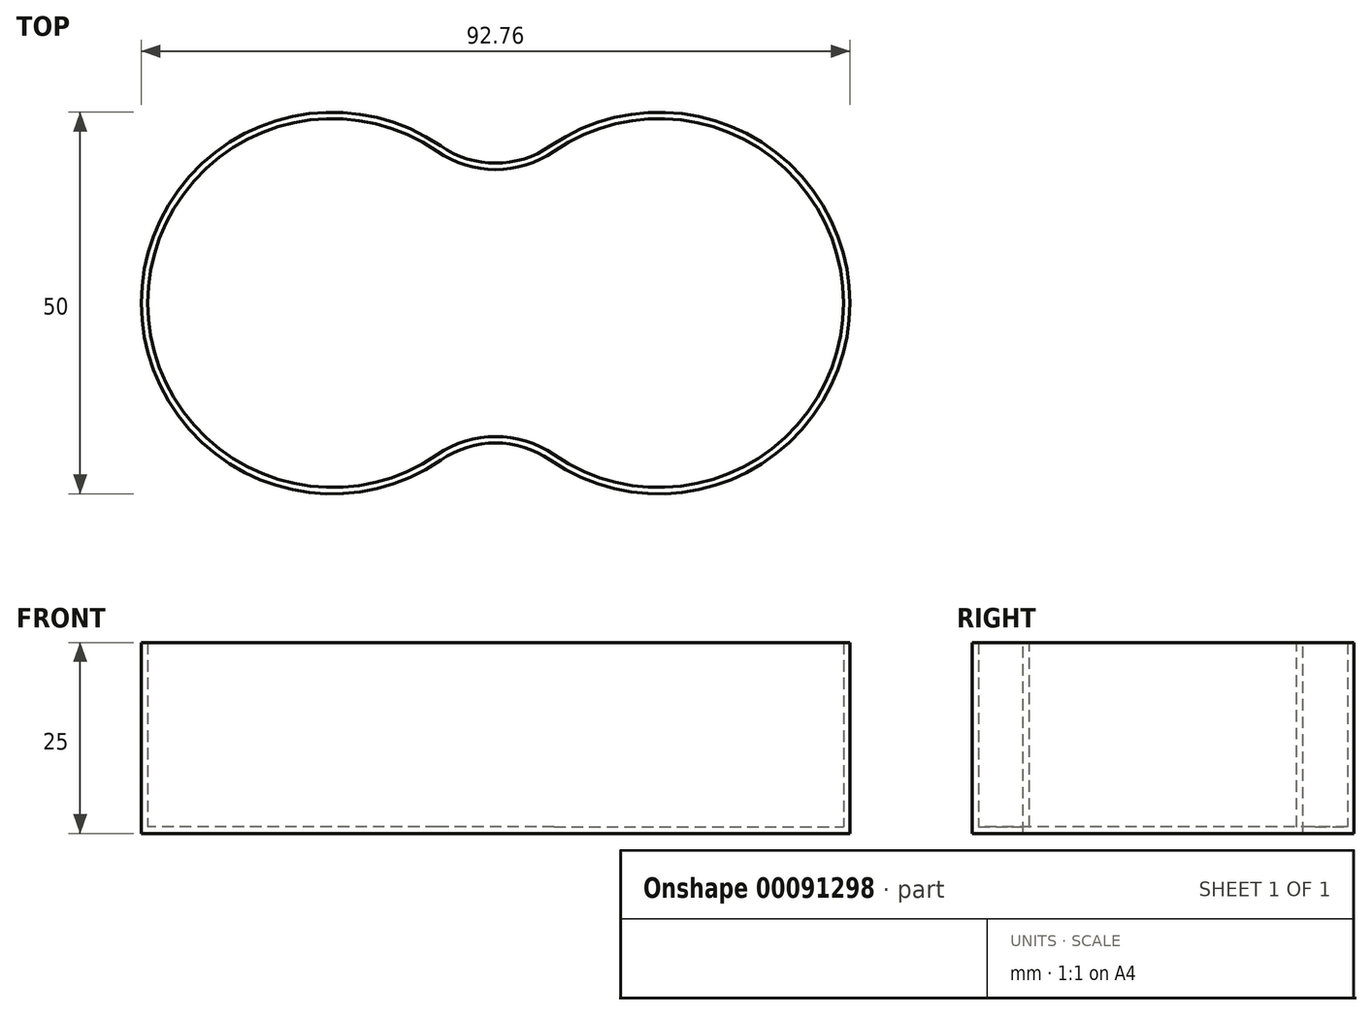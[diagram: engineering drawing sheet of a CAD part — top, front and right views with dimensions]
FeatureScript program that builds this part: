
annotation { "Feature Type Name" : "Feature", "Feature Type Description" : "" }
export const myFeature = defineFeature(function(context is Context, id is Id, definition is map)
    precondition{}
    {
        {
            var Q0;
            Q0=qCreatedBy(makeId("Top.planeOp"),FACE);
            var sketch = newSketch(context, id + "F0", { "sketchPlane" : qUnion([Q0])});
            skCircle(sketch, "E0", {"center": v(-25, 0) * mm, "radius": 25 * mm});
            skCircle(sketch, "E1", {"center": v(17.76, 0) * mm, "radius": 25 * mm});
            skSolve(sketch);
        }
        {
            var Q0;
            Q0=makeQuery(id+"F0.imprint","IMPRINT",FACE,{"disambiguationData":[TD([[makeQuery(id+"F0.imprint","IMPRINT",EDGE,{"derivedFrom":sQuery(id+"F0.wireOp",EDGE,"E0")}),1.0]])]});
            var Q1;
            Q1=makeQuery(id+"F0.imprint","IMPRINT",FACE,{"disambiguationData":[TD([[makeQuery(id+"F0.imprint","IMPRINT",EDGE,{"derivedFrom":sQuery(id+"F0.wireOp",EDGE,"E1")}),1.0]])]});
            var Q2;
            Q2=sQuery(id+"F0.wireOp",EDGE,"E1");
            var Q3;
            Q3=sQuery(id+"F0.wireOp",EDGE,"E0");
            extrude(context, id + "F1", {"entities" : qUnion([Q0, Q1]), "surfaceEntities" : qUnion([Q2, Q3]), "depth" : 25 * mm});
        }
        {
            var Q0;
            {var subQ0=sQuery(id+"F0.wireOp",EDGE,"E1");var subQ1=sQuery(id+"F0.wireOp",EDGE,"E0");Q0=makeQuery(id+"F1.opExtrude","SWEPT_EDGE",EDGE,{"disambiguationData":[OSD([subQ1,subQ0]),TDD([makeQuery(id+"F0.imprint","INTERSECT",VERTEX,{"disambiguationData":[OD(0.0)],"derivedFrom":[subQ1,subQ0]})])]});}
            var Q1;
            {var subQ0=sQuery(id+"F0.wireOp",EDGE,"E1");var subQ1=sQuery(id+"F0.wireOp",EDGE,"E0");Q1=makeQuery(id+"F1.opExtrude","SWEPT_EDGE",EDGE,{"disambiguationData":[OSD([subQ1,subQ0]),TDD([makeQuery(id+"F0.imprint","INTERSECT",VERTEX,{"disambiguationData":[OD(1.0)],"derivedFrom":[subQ1,subQ0]})])]});}
            fillet(context, id + "F2", {"entities" : qUnion([Q0, Q1]), "radius" : 12.62 * mm, "tangentPropagation" : true, "allowEdgeOverflow" : false});
        }
        {
            var Q0;
            Q0=makeQuery(id+"F1.opExtrude","CAP_FACE",FACE,{"disambiguationData":[OSD([sQuery(id+"F0.wireOp",EDGE,"E0"),sQuery(id+"F0.wireOp",EDGE,"E1")])],"isStart":false});
            shell(context, id + "F3", {"entities" : qUnion([Q0]), "thickness" : 0.84 * mm});
        }
    });
